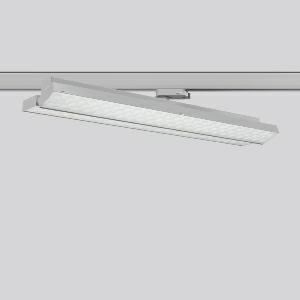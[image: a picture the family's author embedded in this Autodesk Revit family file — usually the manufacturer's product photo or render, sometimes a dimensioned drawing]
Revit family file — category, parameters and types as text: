
# Revit family: tx-move_742163_004_2_9358
name_source: partatom
category: Lighting Fixtures
units: mm (PartAtom-declared; Revit-internal decimal feet)

## family parameters
Cut with Voids When Loaded = No
Host = Face
Light Source = No
Part Type = Normal
Room Calculation Point = No
Round Connector Dimension = Use Diameter
Shared = No

## types (1)
- MultiLumen 1 (1 x LED Modul 927, 2000 lm, 2700)
    Apparent Load = 38 VA
    CIE Flux Codes = 65 90 98 100 100
    Color Rendering = 92
    Color Temperature = 2700
    Default Elevation = 1800 mm
    Description = Series: TX-MOVE
Multifunctional surface-mounted spotlight for area lighting. Very flat design. Housing: sheet steel, powder-coated. Rotation range: 356°. Swivel range: 90°. Consistent alignment possible with visible tilt scale. High-efficiency LED units with optimum light control thanks to clear plastic (PC) lens optics. Spezielle Mikrostrukturen reduzieren Gelbsaum. Asymmetrical light distribution. Best colour rendering with CRI >90 for fresh products and coloured textiles. With multi adaptor for 3-circuit tracks 230 V. Suitable for Track on ceiling. MultiLumen: Luminous flux adjustable in 3 steps. Factory setting is the highest luminous flux. Environmentally friendly and resource-saving due to replaceable and recyclable components. 
Colour: silver, matt (approx. RAL 9006)
Length: 570 mm
Width: 119 mm
Height: 92 mm
Lamp: LED
Socket: without socket
Colour temperature: 2700K
Colour rendering index (CRI): 90
System power: 38 W
Rated luminous flux: 4000 lm
Luminous efficiency: 105 lm/W
System power 2: 51 W
Rated luminous flux 2: 5250 lm
Luminous efficiency 2: 103 lm/W
System power 3: 62 W
Rated luminous flux 3: 6200 lm
Luminous efficiency 3: 100 lm/W
Control gear: Regulated power supply
Protection class: I
Type of protection: IP 20
    Height = 75 mm
    Lamp = 1 x LED Modul 927
    Lamp Light Flux = 2000 lm
    Lamp count = 1
    Length = 569 mm
    Lifetime = 50000 h
    Luminous efficacy = 105 lm/W
    Manufacturer = RZB
    ModVariant = No
    Model = 742163.004.2
    Mounting Place = Ceiling
    Mounting Type = Surface mounted
    Number of Poles = 1
    OnlyDefault = Yes
    Power Factor = 1
    Product Name = TX-MOVE
    Product group = Track mounted projectors
    ProductGroupID = 301
    Protection Class = Protection class I
    Protection Degree = IP 20
    RLX_Detail_Level = 1
    RLX_Emergency_Light_Flux = 0 lm
    RLX_Emergency_Type = 0
    RLX_Emergency_Type_DB = No
    RlxData = <blob elided: 53913 chars, md5=1cbe4f74>
    Socket = socket
    Standby Power = 0 W
    System Light Flux = 4000 lm
    System Power = 38 W
    Type Comments = MultiLumen 1
    Type Image = 742162.004.jpg
    URL = http://relux.com
    VarID = multilumen_1
    Voltage = 0 V
    Weight = 0.00 kg
    Width = 119 mm

## geometry (parser evidence)
native form markers: Blend x4, Sweep x14
no freeform markers — native parametric forms only
